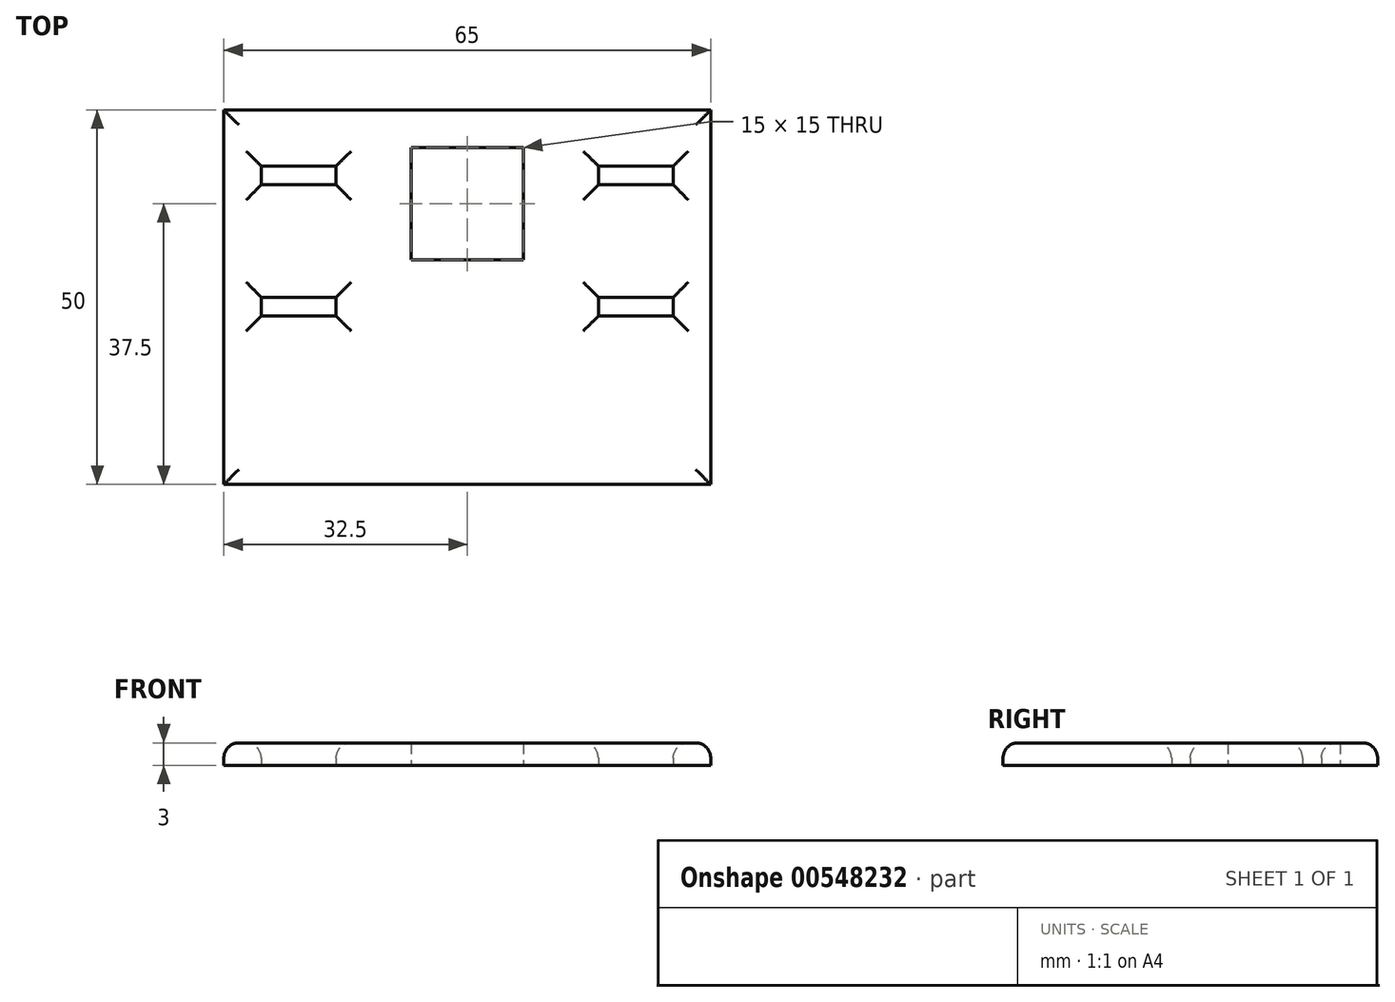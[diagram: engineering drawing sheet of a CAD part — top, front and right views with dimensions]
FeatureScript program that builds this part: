
annotation { "Feature Type Name" : "Feature", "Feature Type Description" : "" }
export const myFeature = defineFeature(function(context is Context, id is Id, definition is map)
    precondition{}
    {
        {
            var Q0;
            Q0=qCreatedBy(makeId("Top.planeOp"),FACE);
            var sketch = newSketch(context, id + "F0", { "sketchPlane" : qUnion([Q0])});
            skLineSegment(sketch, "E0.bottom", {"start": v(32.5, 25) * mm, "end": v(-32.5, 25) * mm});
            skLineSegment(sketch, "E0.top", {"start": v(32.5, -25) * mm, "end": v(-32.5, -25) * mm});
            skLineSegment(sketch, "E0.left", {"start": v(32.5, 25) * mm, "end": v(32.5, -25) * mm});
            skLineSegment(sketch, "E0.right", {"start": v(-32.5, 25) * mm, "end": v(-32.5, -25) * mm});
            skPoint(sketch, "E0.middle", {"position": v(0, 0) * mm});
            skLineSegment(sketch, "E1.bottom", {"start": v(-7.5, 20) * mm, "end": v(7.5, 20) * mm});
            skLineSegment(sketch, "E1.top", {"start": v(-7.5, 5) * mm, "end": v(7.5, 5) * mm});
            skLineSegment(sketch, "E1.left", {"start": v(-7.5, 20) * mm, "end": v(-7.5, 5) * mm});
            skLineSegment(sketch, "E1.right", {"start": v(7.5, 20) * mm, "end": v(7.5, 5) * mm});
            skLineSegment(sketch, "E2", {"start": v(-7.5, 20) * mm, "end": v(-7.5, 25) * mm, "construction": true});
            skLineSegment(sketch, "E3", {"start": v(-7.5, 20) * mm, "end": v(-32.5, 20) * mm, "construction": true});
            skLineSegment(sketch, "E4", {"start": v(7.5, 20) * mm, "end": v(32.5, 20) * mm, "construction": true});
            skLineSegment(sketch, "E5.bottom", {"start": v(27.5, 0) * mm, "end": v(17.5, 0) * mm});
            skLineSegment(sketch, "E5.top", {"start": v(27.5, -2.5) * mm, "end": v(17.5, -2.5) * mm});
            skLineSegment(sketch, "E5.left", {"start": v(27.5, 0) * mm, "end": v(27.5, -2.5) * mm});
            skLineSegment(sketch, "E5.right", {"start": v(17.5, 0) * mm, "end": v(17.5, -2.5) * mm});
            skLineSegment(sketch, "E6.bottom", {"start": v(-17.5, 0) * mm, "end": v(-27.5, 0) * mm});
            skLineSegment(sketch, "E6.top", {"start": v(-17.5, -2.5) * mm, "end": v(-27.5, -2.5) * mm});
            skLineSegment(sketch, "E6.left", {"start": v(-17.5, 0) * mm, "end": v(-17.5, -2.5) * mm});
            skLineSegment(sketch, "E6.right", {"start": v(-27.5, 0) * mm, "end": v(-27.5, -2.5) * mm});
            skLineSegment(sketch, "E7.bottom", {"start": v(-17.5, 17.5) * mm, "end": v(-27.5, 17.5) * mm});
            skLineSegment(sketch, "E7.top", {"start": v(-17.5, 15) * mm, "end": v(-27.5, 15) * mm});
            skLineSegment(sketch, "E7.left", {"start": v(-17.5, 17.5) * mm, "end": v(-17.5, 15) * mm});
            skLineSegment(sketch, "E7.right", {"start": v(-27.5, 17.5) * mm, "end": v(-27.5, 15) * mm});
            skLineSegment(sketch, "E8", {"start": v(-17.5, -2.5) * mm, "end": v(-17.5, -25) * mm, "construction": true});
            skLineSegment(sketch, "E9", {"start": v(27.5, -2.5) * mm, "end": v(27.5, -25) * mm, "construction": true});
            skLineSegment(sketch, "E10", {"start": v(-27.5, -2.5) * mm, "end": v(-32.5, -2.5) * mm, "construction": true});
            skLineSegment(sketch, "E11", {"start": v(27.5, -2.5) * mm, "end": v(32.5, -2.5) * mm, "construction": true});
            skLineSegment(sketch, "E12", {"start": v(-27.5, 17.5) * mm, "end": v(-32.5, 17.5) * mm, "construction": true});
            skLineSegment(sketch, "E13", {"start": v(-17.5, 17.5) * mm, "end": v(-17.5, 25) * mm, "construction": true});
            skLineSegment(sketch, "E14.bottom", {"start": v(27.5, 17.5) * mm, "end": v(17.5, 17.5) * mm});
            skLineSegment(sketch, "E14.top", {"start": v(27.5, 15) * mm, "end": v(17.5, 15) * mm});
            skLineSegment(sketch, "E14.left", {"start": v(27.5, 17.5) * mm, "end": v(27.5, 15) * mm});
            skLineSegment(sketch, "E14.right", {"start": v(17.5, 17.5) * mm, "end": v(17.5, 15) * mm});
            skLineSegment(sketch, "E15", {"start": v(27.5, 17.5) * mm, "end": v(32.5, 17.5) * mm, "construction": true});
            skLineSegment(sketch, "E16", {"start": v(27.5, 17.5) * mm, "end": v(27.5, 25) * mm, "construction": true});
            skLineSegment(sketch, "E17", {"start": v(-27.5, 15) * mm, "end": v(-27.5, 0) * mm, "construction": true});
            skLineSegment(sketch, "E18", {"start": v(17.5, 15) * mm, "end": v(17.5, 0) * mm, "construction": true});
            skSolve(sketch);
        }
        {
            var Q0;
            Q0 = qSketchRegion(id + "F0", true);
            extrude(context, id + "F1", {"entities" : qUnion([Q0]), "depth" : 3 * mm, "offsetDistance" : 25 * mm});
        }
        {
            var Q0;
            Q0=makeQuery(id+"F1.opExtrude","CAP_EDGE",EDGE,{"disambiguationData":[OSD([sQuery(id+"F0.wireOp",EDGE,"E7.bottom")])],"isStart":false});
            var Q1;
            Q1=makeQuery(id+"F1.opExtrude","CAP_EDGE",EDGE,{"disambiguationData":[OSD([sQuery(id+"F0.wireOp",EDGE,"E7.top")])],"isStart":false});
            var Q2;
            Q2=makeQuery(id+"F1.opExtrude","CAP_EDGE",EDGE,{"disambiguationData":[OSD([sQuery(id+"F0.wireOp",EDGE,"E7.right")])],"isStart":false});
            var Q3;
            Q3=makeQuery(id+"F1.opExtrude","CAP_EDGE",EDGE,{"disambiguationData":[OSD([sQuery(id+"F0.wireOp",EDGE,"E7.left")])],"isStart":false});
            var Q4;
            Q4=makeQuery(id+"F1.opExtrude","CAP_EDGE",EDGE,{"disambiguationData":[OSD([sQuery(id+"F0.wireOp",EDGE,"E0.bottom")])],"isStart":false});
            var Q5;
            Q5=makeQuery(id+"F1.opExtrude","CAP_EDGE",EDGE,{"disambiguationData":[OSD([sQuery(id+"F0.wireOp",EDGE,"E0.right")])],"isStart":false});
            var Q6;
            Q6=makeQuery(id+"F1.opExtrude","CAP_EDGE",EDGE,{"disambiguationData":[OSD([sQuery(id+"F0.wireOp",EDGE,"E6.top")])],"isStart":false});
            var Q7;
            Q7=makeQuery(id+"F1.opExtrude","CAP_EDGE",EDGE,{"disambiguationData":[OSD([sQuery(id+"F0.wireOp",EDGE,"E0.top")])],"isStart":false});
            var Q8;
            Q8=makeQuery(id+"F1.opExtrude","CAP_EDGE",EDGE,{"disambiguationData":[OSD([sQuery(id+"F0.wireOp",EDGE,"E6.bottom")])],"isStart":false});
            var Q9;
            Q9=makeQuery(id+"F1.opExtrude","CAP_EDGE",EDGE,{"disambiguationData":[OSD([sQuery(id+"F0.wireOp",EDGE,"E6.right")])],"isStart":false});
            var Q10;
            Q10=makeQuery(id+"F1.opExtrude","CAP_EDGE",EDGE,{"disambiguationData":[OSD([sQuery(id+"F0.wireOp",EDGE,"E6.left")])],"isStart":false});
            var Q11;
            Q11=makeQuery(id+"F1.opExtrude","CAP_EDGE",EDGE,{"disambiguationData":[OSD([sQuery(id+"F0.wireOp",EDGE,"E14.top")])],"isStart":false});
            var Q12;
            Q12=makeQuery(id+"F1.opExtrude","CAP_EDGE",EDGE,{"disambiguationData":[OSD([sQuery(id+"F0.wireOp",EDGE,"E14.bottom")])],"isStart":false});
            var Q13;
            Q13=makeQuery(id+"F1.opExtrude","CAP_EDGE",EDGE,{"disambiguationData":[OSD([sQuery(id+"F0.wireOp",EDGE,"E14.right")])],"isStart":false});
            var Q14;
            Q14=makeQuery(id+"F1.opExtrude","CAP_EDGE",EDGE,{"disambiguationData":[OSD([sQuery(id+"F0.wireOp",EDGE,"E14.left")])],"isStart":false});
            var Q15;
            Q15=makeQuery(id+"F1.opExtrude","CAP_EDGE",EDGE,{"disambiguationData":[OSD([sQuery(id+"F0.wireOp",EDGE,"E0.left")])],"isStart":false});
            var Q16;
            Q16=makeQuery(id+"F1.opExtrude","CAP_EDGE",EDGE,{"disambiguationData":[OSD([sQuery(id+"F0.wireOp",EDGE,"E5.bottom")])],"isStart":false});
            var Q17;
            Q17=makeQuery(id+"F1.opExtrude","CAP_EDGE",EDGE,{"disambiguationData":[OSD([sQuery(id+"F0.wireOp",EDGE,"E5.right")])],"isStart":false});
            var Q18;
            Q18=makeQuery(id+"F1.opExtrude","CAP_EDGE",EDGE,{"disambiguationData":[OSD([sQuery(id+"F0.wireOp",EDGE,"E5.top")])],"isStart":false});
            var Q19;
            Q19=makeQuery(id+"F1.opExtrude","CAP_EDGE",EDGE,{"disambiguationData":[OSD([sQuery(id+"F0.wireOp",EDGE,"E5.left")])],"isStart":false});
            fillet(context, id + "F2", {"entities" : qUnion([Q0, Q1, Q2, Q3, Q4, Q5, Q6, Q7, Q8, Q9, Q10, Q11, Q12, Q13, Q14, Q15, Q16, Q17, Q18, Q19]), "radius" : 2 * mm, "tangentPropagation" : true, "allowEdgeOverflow" : false});
        }
    });
